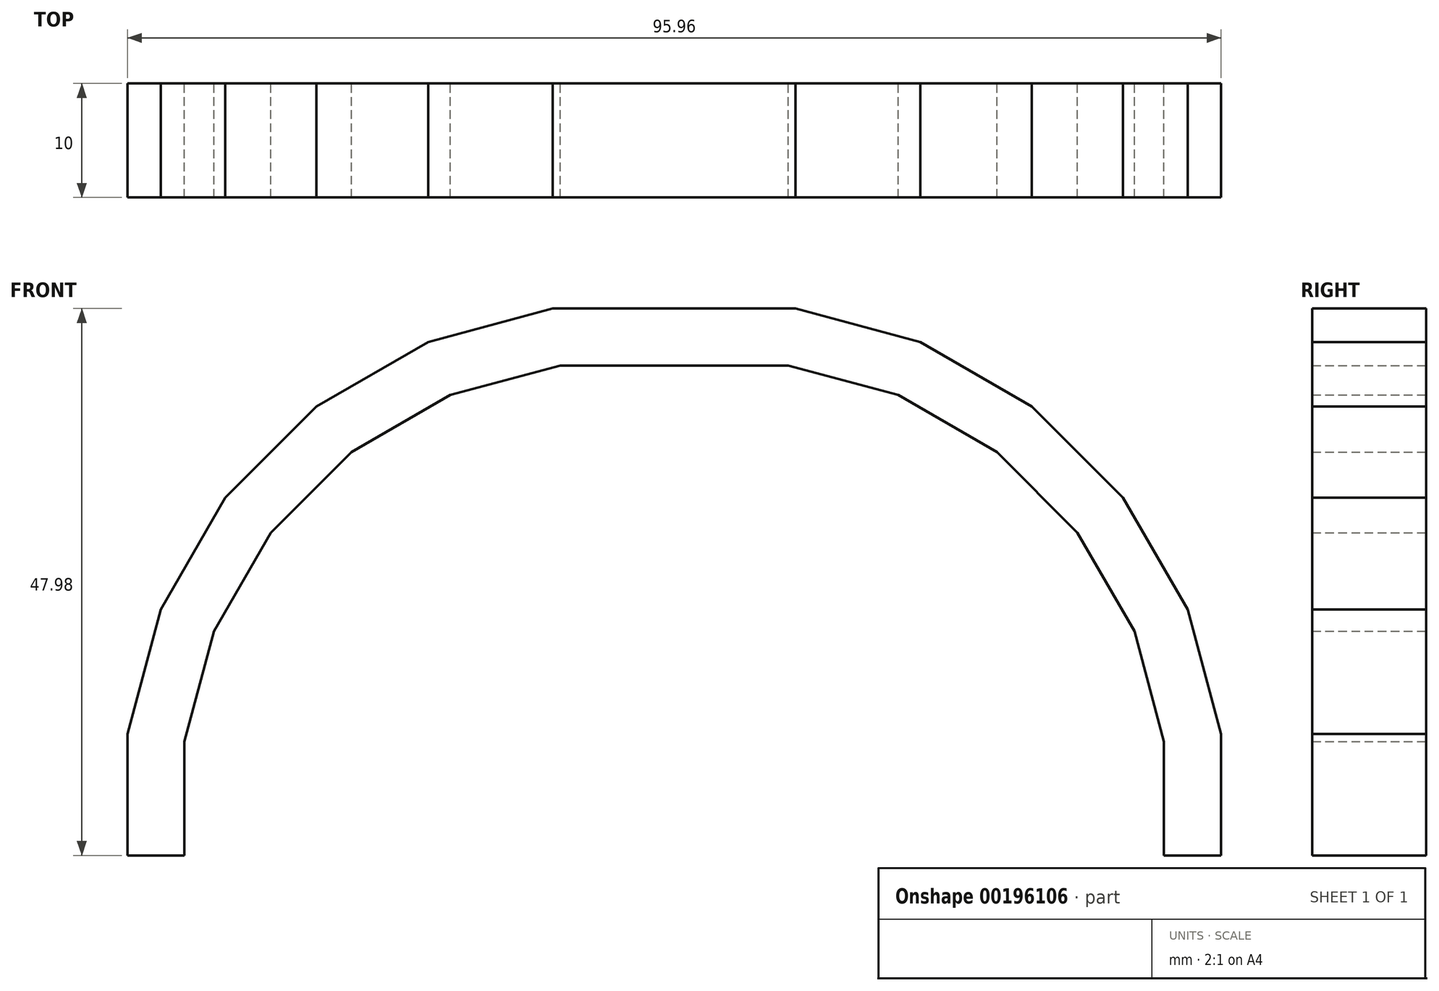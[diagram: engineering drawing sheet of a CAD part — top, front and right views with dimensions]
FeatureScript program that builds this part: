
annotation { "Feature Type Name" : "Feature", "Feature Type Description" : "" }
export const myFeature = defineFeature(function(context is Context, id is Id, definition is map)
    precondition{}
    {
        {
            var Q0;
            Q0=qCreatedBy(makeId("Front.planeOp"),FACE);
            var sketch = newSketch(context, id + "F0", { "sketchPlane" : qUnion([Q0])});
            skLineSegment(sketch, "E0", {"start": v(5, 0) * mm, "end": v(5, 10) * mm});
            skLineSegment(sketch, "E1", {"start": v(5, 10) * mm, "end": v(7.59, 19.66) * mm});
            skLineSegment(sketch, "E2", {"start": v(7.59, 19.66) * mm, "end": v(12.59, 28.32) * mm});
            skLineSegment(sketch, "E3", {"start": v(12.59, 28.32) * mm, "end": v(19.66, 35.4) * mm});
            skLineSegment(sketch, "E4", {"start": v(19.66, 35.4) * mm, "end": v(28.32, 40.4) * mm});
            skLineSegment(sketch, "E5", {"start": v(28.32, 40.4) * mm, "end": v(37.98, 42.98) * mm});
            skLineSegment(sketch, "E6", {"start": v(37.98, 42.98) * mm, "end": v(47.98, 42.98) * mm});
            skLineSegment(sketch, "E7.0", {"start": v(37.32, 47.98) * mm, "end": v(47.98, 47.98) * mm});
            skLineSegment(sketch, "E7.1", {"start": v(26.39, 45.05) * mm, "end": v(37.32, 47.98) * mm});
            skLineSegment(sketch, "E7.2", {"start": v(16.59, 39.4) * mm, "end": v(26.39, 45.05) * mm});
            skLineSegment(sketch, "E7.3", {"start": v(0, 0) * mm, "end": v(0, 10.66) * mm});
            skLineSegment(sketch, "E7.4", {"start": v(0, 10.66) * mm, "end": v(2.93, 21.59) * mm});
            skLineSegment(sketch, "E7.5", {"start": v(2.93, 21.59) * mm, "end": v(8.59, 31.39) * mm});
            skLineSegment(sketch, "E7.6", {"start": v(8.59, 31.39) * mm, "end": v(16.59, 39.4) * mm});
            skLineSegment(sketch, "E8", {"start": v(5, 0) * mm, "end": v(0, 0) * mm});
            skLineSegment(sketch, "E9", {"start": v(47.98, 47.98) * mm, "end": v(47.98, 42.98) * mm});
            skSolve(sketch);
        }
        {
            var Q0;
            Q0=makeQuery(id+"F0.imprint","IMPRINT",FACE,{"disambiguationData":[TD([[makeQuery(id+"F0.imprint","IMPRINT",EDGE,{"derivedFrom":sQuery(id+"F0.wireOp",EDGE,"E0")}),1.0]])]});
            extrude(context, id + "F1", {"entities" : qUnion([Q0]), "depth" : 10 * mm});
        }
        {
            var Q0;
            Q0=makeQuery(id+"F1.opExtrude","SWEPT_BODY",BODY,{"disambiguationData":[OSD([sQuery(id+"F0.wireOp",EDGE,"E0"),sQuery(id+"F0.wireOp",EDGE,"E1"),sQuery(id+"F0.wireOp",EDGE,"E2"),sQuery(id+"F0.wireOp",EDGE,"E3"),sQuery(id+"F0.wireOp",EDGE,"E4"),sQuery(id+"F0.wireOp",EDGE,"E5"),sQuery(id+"F0.wireOp",EDGE,"E6"),sQuery(id+"F0.wireOp",EDGE,"E7.0"),sQuery(id+"F0.wireOp",EDGE,"E7.1"),sQuery(id+"F0.wireOp",EDGE,"E7.2"),sQuery(id+"F0.wireOp",EDGE,"E7.3"),sQuery(id+"F0.wireOp",EDGE,"E7.4"),sQuery(id+"F0.wireOp",EDGE,"E7.5"),sQuery(id+"F0.wireOp",EDGE,"E7.6"),sQuery(id+"F0.wireOp",EDGE,"E8"),sQuery(id+"F0.wireOp",EDGE,"E9")])]});
            var Q1;
            Q1=makeQuery(id+"F1.opExtrude","SWEPT_FACE",FACE,{"disambiguationData":[OSD([sQuery(id+"F0.wireOp",EDGE,"E9")])]});
            mirror(context, id + "F2", {"operationType" : NewBodyOperationType.ADD, "entities" : qUnion([Q0]), "mirrorPlane" : qUnion([Q1])});
        }
    });
